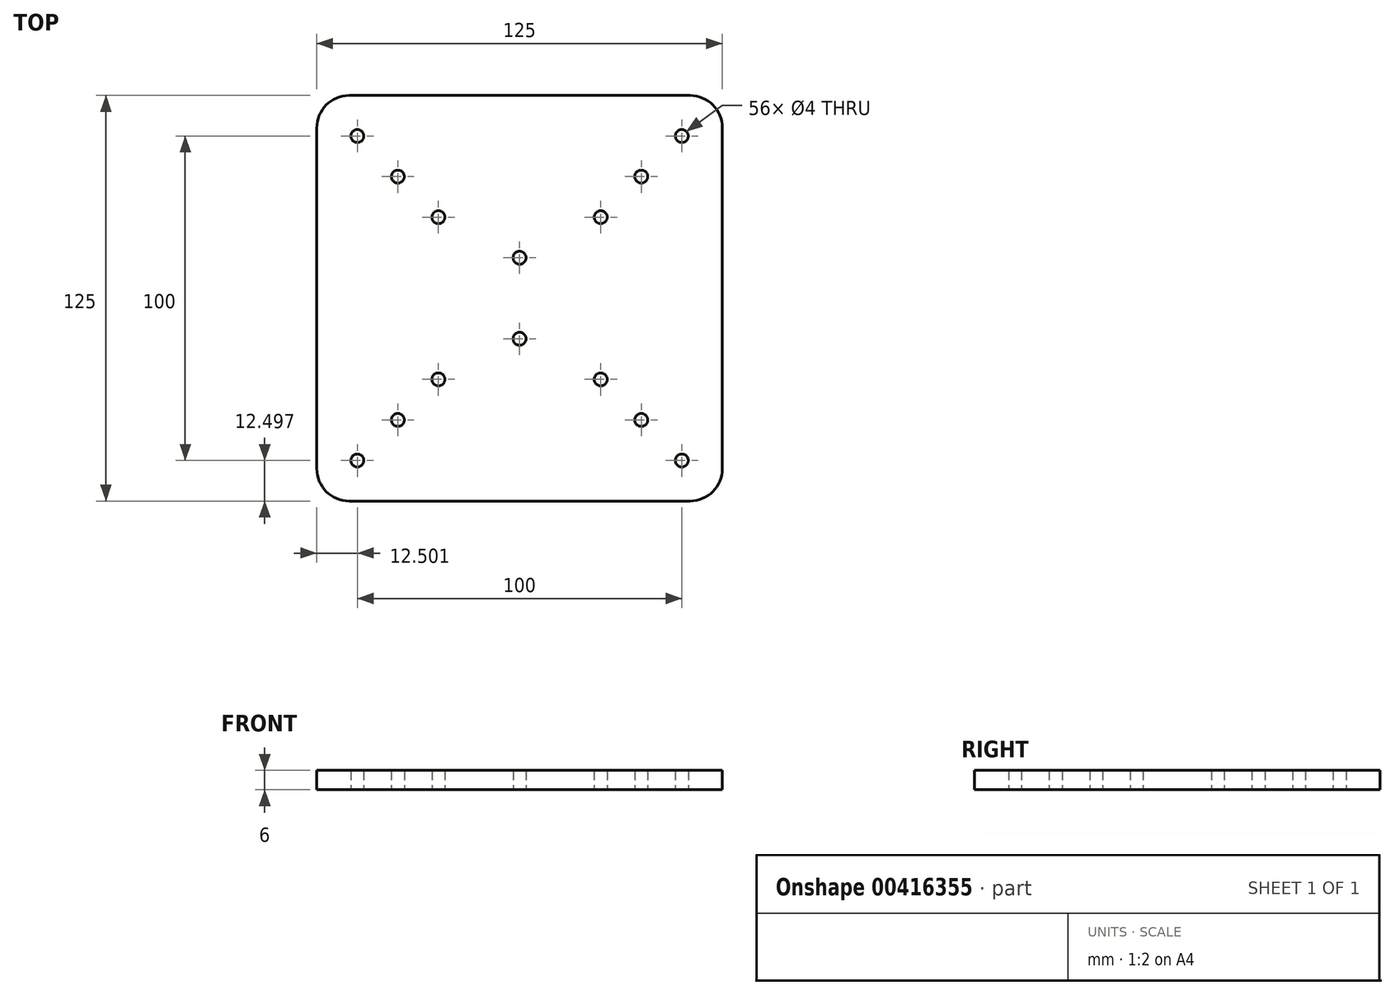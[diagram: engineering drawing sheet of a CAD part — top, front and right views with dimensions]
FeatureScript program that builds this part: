
annotation { "Feature Type Name" : "Feature", "Feature Type Description" : "" }
export const myFeature = defineFeature(function(context is Context, id is Id, definition is map)
    precondition{}
    {
        {
            var Q0;
            Q0=qCreatedBy(makeId("Top.planeOp"),FACE);
            var sketch = newSketch(context, id + "F0", { "sketchPlane" : qUnion([Q0])});
            skLineSegment(sketch, "E0.bottom", {"start": v(-54.27, 76.18) * mm, "end": v(70.73, 76.18) * mm});
            skLineSegment(sketch, "E0.top", {"start": v(-54.27, -48.82) * mm, "end": v(70.73, -48.82) * mm});
            skLineSegment(sketch, "E0.left", {"start": v(-54.27, 76.18) * mm, "end": v(-54.27, -48.82) * mm});
            skLineSegment(sketch, "E0.right", {"start": v(70.73, 76.18) * mm, "end": v(70.73, -48.82) * mm});
            skCircle(sketch, "E1", {"center": v(-41.77, -36.32) * mm, "radius": 2 * mm});
            skCircle(sketch, "E2", {"center": v(58.23, -36.32) * mm, "radius": 2 * mm});
            skCircle(sketch, "E3", {"center": v(-41.77, 63.68) * mm, "radius": 2 * mm});
            skCircle(sketch, "E4", {"center": v(58.23, 63.68) * mm, "radius": 2 * mm});
            skCircle(sketch, "E5", {"center": v(-29.27, -23.82) * mm, "radius": 2 * mm});
            skCircle(sketch, "E6", {"center": v(45.73, -23.82) * mm, "radius": 2 * mm});
            skCircle(sketch, "E7", {"center": v(-29.27, 51.18) * mm, "radius": 2 * mm});
            skCircle(sketch, "E8", {"center": v(45.73, 51.18) * mm, "radius": 2 * mm});
            skCircle(sketch, "E9", {"center": v(-16.77, 38.68) * mm, "radius": 2 * mm});
            skCircle(sketch, "E10", {"center": v(33.23, 38.68) * mm, "radius": 2 * mm});
            skCircle(sketch, "E11", {"center": v(-16.77, -11.32) * mm, "radius": 2 * mm});
            skCircle(sketch, "E12", {"center": v(33.23, -11.32) * mm, "radius": 2 * mm});
            skCircle(sketch, "E13", {"center": v(8.23, 1.18) * mm, "radius": 2 * mm});
            skCircle(sketch, "E14", {"center": v(8.23, 26.18) * mm, "radius": 2 * mm});
            skSolve(sketch);
        }
        {
            var Q0;
            Q0 = qSketchRegion(id + "F0", true);
            extrude(context, id + "F1", {"entities" : qUnion([Q0]), "depth" : 6 * mm});
        }
        {
            var Q0;
            Q0=makeQuery(id+"F1.opExtrude","SWEPT_EDGE",EDGE,{"disambiguationData":[OSD([sQuery(id+"F0.wireOp",EDGE,"E0.bottom"),sQuery(id+"F0.wireOp",EDGE,"E0.left")])]});
            var Q1;
            Q1=makeQuery(id+"F1.opExtrude","SWEPT_EDGE",EDGE,{"disambiguationData":[OSD([sQuery(id+"F0.wireOp",EDGE,"E0.top"),sQuery(id+"F0.wireOp",EDGE,"E0.left")])]});
            var Q2;
            Q2=makeQuery(id+"F1.opExtrude","SWEPT_EDGE",EDGE,{"disambiguationData":[OSD([sQuery(id+"F0.wireOp",EDGE,"E0.top"),sQuery(id+"F0.wireOp",EDGE,"E0.right")])]});
            var Q3;
            Q3=makeQuery(id+"F1.opExtrude","SWEPT_EDGE",EDGE,{"disambiguationData":[OSD([sQuery(id+"F0.wireOp",EDGE,"E0.bottom"),sQuery(id+"F0.wireOp",EDGE,"E0.right")])]});
            fillet(context, id + "F2", {"entities" : qUnion([Q0, Q1, Q2, Q3]), "radius" : 10 * mm, "tangentPropagation" : true, "allowEdgeOverflow" : false});
        }
    });
